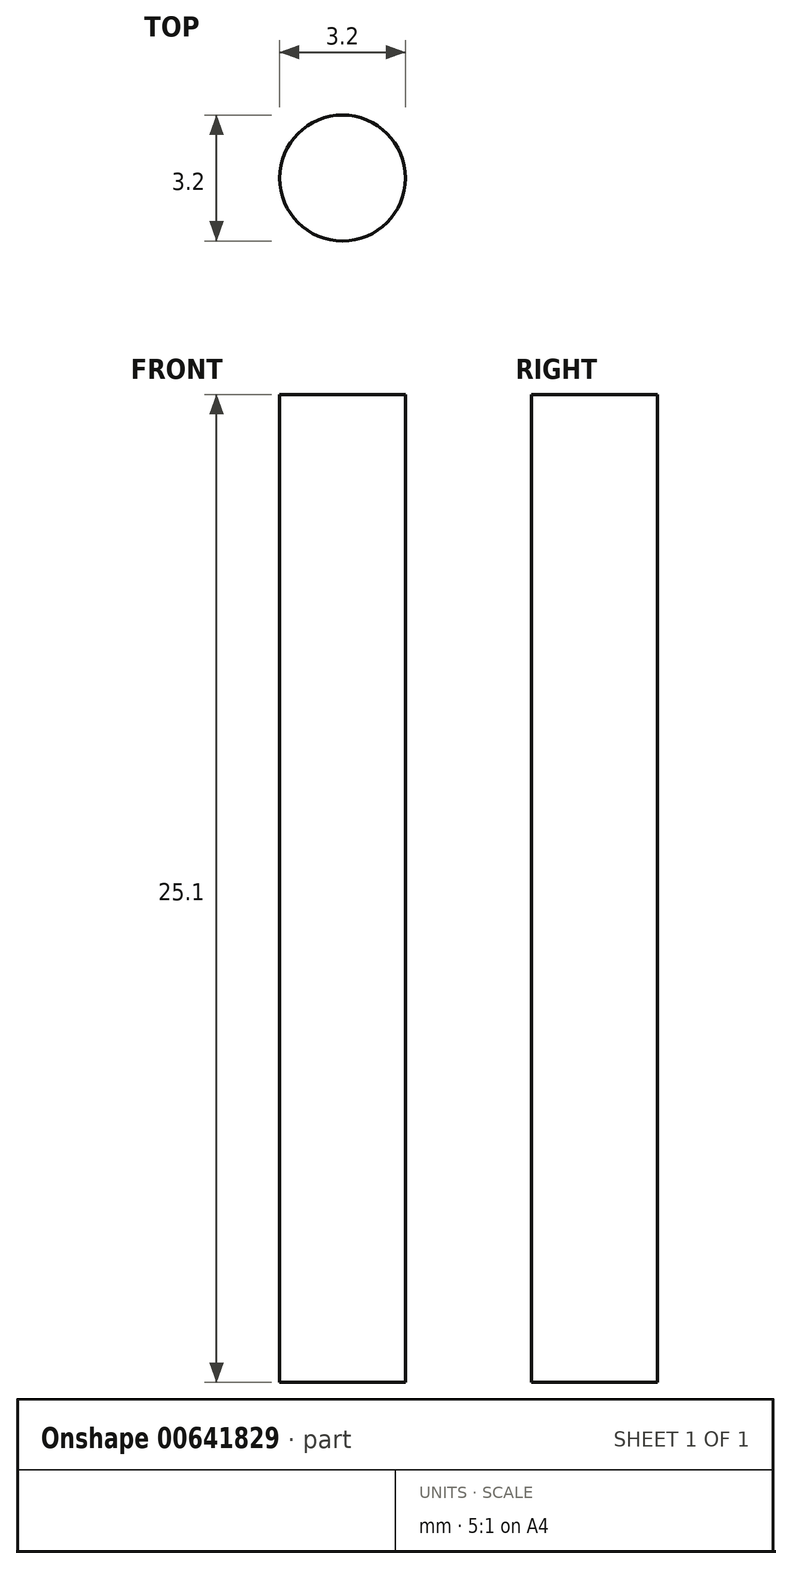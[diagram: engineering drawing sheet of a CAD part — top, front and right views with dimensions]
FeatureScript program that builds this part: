
annotation { "Feature Type Name" : "Feature", "Feature Type Description" : "" }
export const myFeature = defineFeature(function(context is Context, id is Id, definition is map)
    precondition{}
    {
        {
            var Q0;
            Q0=qCreatedBy(makeId("Top.planeOp"),FACE);
            var sketch = newSketch(context, id + "F0", { "sketchPlane" : qUnion([Q0])});
            skCircle(sketch, "E0", {"center": v(0, 0) * mm, "radius": 1.6 * mm});
            skSolve(sketch);
        }
        {
            var Q0;
            Q0 = qSketchRegion(id + "F0", true);
            extrude(context, id + "F1", {"entities" : qUnion([Q0]), "depth" : 25.1 * mm, "offsetDistance" : 25 * mm});
        }
    });
